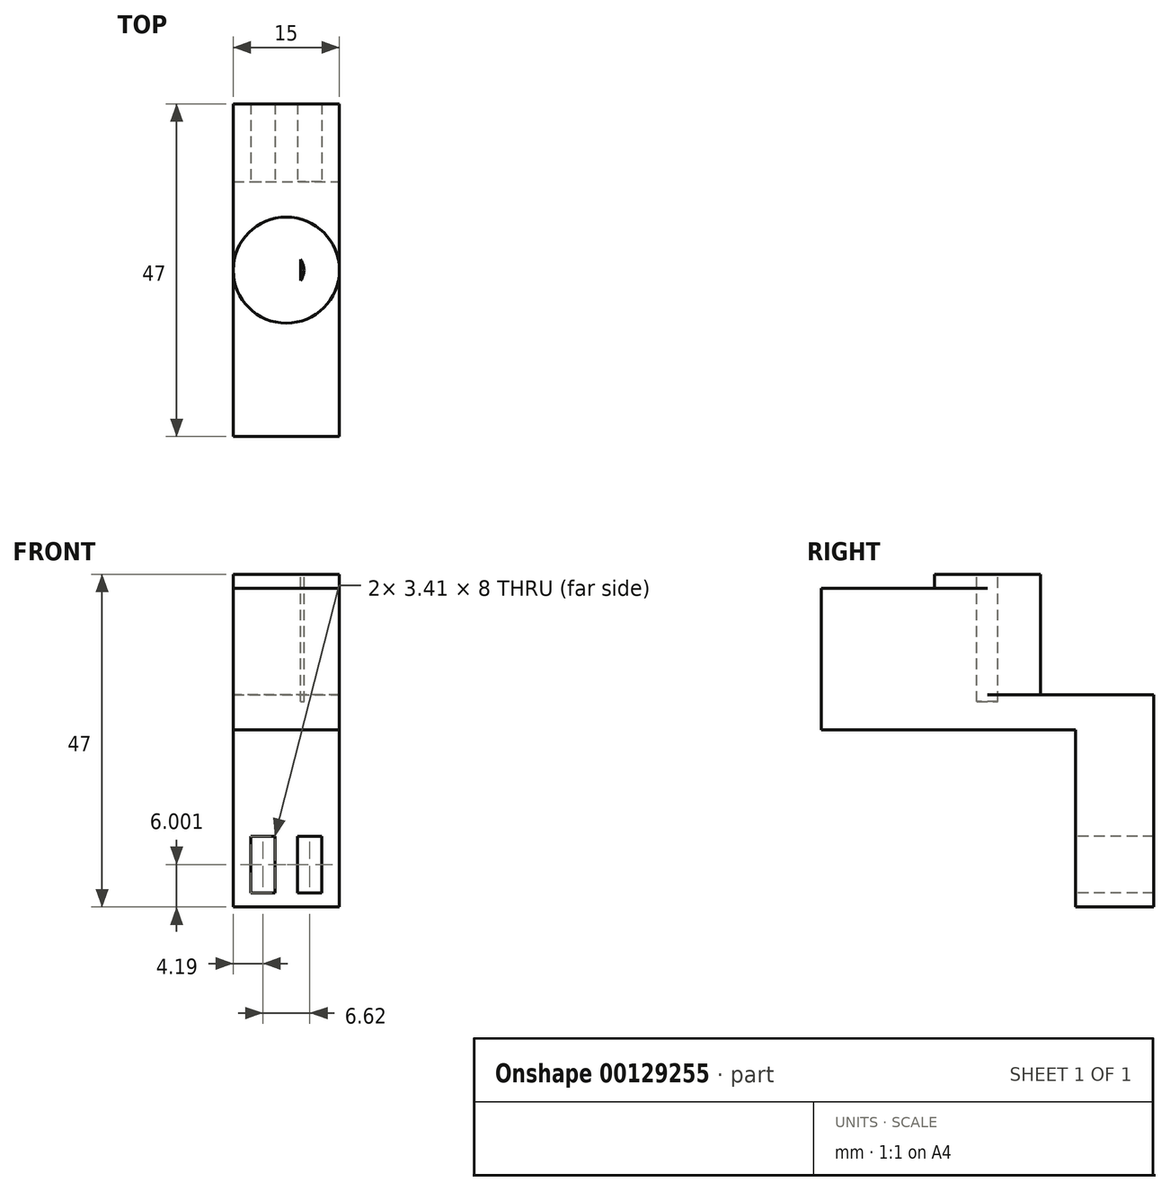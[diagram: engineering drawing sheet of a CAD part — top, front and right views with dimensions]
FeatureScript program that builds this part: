
annotation { "Feature Type Name" : "Feature", "Feature Type Description" : "" }
export const myFeature = defineFeature(function(context is Context, id is Id, definition is map)
    precondition{}
    {
        {
            var Q0;
            Q0=qCreatedBy(makeId("Top.planeOp"),FACE);
            var sketch = newSketch(context, id + "F0", { "sketchPlane" : qUnion([Q0])});
            skCircle(sketch, "E0", {"center": v(0, 0) * mm, "radius": 7.5 * mm});
            skSolve(sketch);
        }
        {
            var Q0;
            Q0=makeQuery(id+"F0.imprint","IMPRINT",FACE,{"disambiguationData":[TD([[makeQuery(id+"F0.imprint","IMPRINT",EDGE,{"derivedFrom":sQuery(id+"F0.wireOp",EDGE,"E0")}),1.0]])]});
            extrude(context, id + "F1", {"entities" : qUnion([Q0]), "depth" : 22 * mm});
        }
        {
            var Q0;
            Q0=makeQuery(id+"F1.opExtrude","CAP_FACE",FACE,{"disambiguationData":[OSD([sQuery(id+"F0.wireOp",EDGE,"E0")])],"isStart":false});
            var sketch = newSketch(context, id + "F2", { "sketchPlane" : qUnion([Q0])});
            skCircle(sketch, "E1", {"center": v(0, 0) * mm, "radius": 2.5 * mm});
            skLineSegment(sketch, "E2.bottom", {"start": v(2, 2.49) * mm, "end": v(3.01, 2.49) * mm});
            skLineSegment(sketch, "E2.top", {"start": v(2, -2.5) * mm, "end": v(3.01, -2.5) * mm});
            skLineSegment(sketch, "E2.left", {"start": v(2, 2.49) * mm, "end": v(2, -2.5) * mm});
            skLineSegment(sketch, "E2.right", {"start": v(3.01, 2.49) * mm, "end": v(3.01, -2.5) * mm});
            skSolve(sketch);
        }
        {
            var Q0;
            {var subQ0=sQuery(id+"F2.wireOp",EDGE,"E2.left");var subQ1=sQuery(id+"F2.wireOp",EDGE,"E1");var subQ2=makeQuery(id+"F2.imprint","INTERSECT",VERTEX,{"disambiguationData":[OD(0.0)],"derivedFrom":[subQ1,subQ0]});Q0=makeQuery(id+"F2.imprint","IMPRINT",FACE,{"disambiguationData":[TD([[makeQuery(id+"F2.imprint","IMPRINT",EDGE,{"disambiguationData":[TD([[subQ2,-1.0]])],"derivedFrom":subQ1}),1.0]])]});}
            extrude(context, id + "F3", {"entities" : qUnion([Q0]), "operationType" : NewBodyOperationType.REMOVE, "oppositeDirection" : true, "depth" : 18 * mm});
        }
        {
            var Q0;
            Q0=makeQuery(id+"F1.opExtrude","CAP_FACE",FACE,{"disambiguationData":[OSD([sQuery(id+"F0.wireOp",EDGE,"E0")])],"isStart":true});
            var sketch = newSketch(context, id + "F4", { "sketchPlane" : qUnion([Q0])});
            skLineSegment(sketch, "E3.bottom", {"start": v(-7.5, 0) * mm, "end": v(7.5, 0) * mm});
            skLineSegment(sketch, "E3.top", {"start": v(-7.5, -23.5) * mm, "end": v(7.5, -23.5) * mm});
            skLineSegment(sketch, "E3.left", {"start": v(-7.5, 0) * mm, "end": v(-7.5, -23.5) * mm});
            skLineSegment(sketch, "E3.right", {"start": v(7.5, 0) * mm, "end": v(7.5, -23.5) * mm});
            skLineSegment(sketch, "E4", {"start": v(-7.5, -12.48) * mm, "end": v(7.5, -12.48) * mm});
            skLineSegment(sketch, "E5.MirrorCS", {"start": v(-7.5, 12.48) * mm, "end": v(7.5, 12.48) * mm});
            skLineSegment(sketch, "E6.MirrorCS", {"start": v(-7.5, 23.5) * mm, "end": v(7.5, 23.5) * mm});
            skLineSegment(sketch, "E7.MirrorCS", {"start": v(7.5, 0) * mm, "end": v(7.5, 23.5) * mm});
            skLineSegment(sketch, "E8.MirrorCS", {"start": v(-7.5, 0) * mm, "end": v(-7.5, 23.5) * mm});
            skSolve(sketch);
        }
        {
            var Q0;
            {var subQ4=sQuery(id+"F4.wireOp",EDGE,"E4");Q0=makeQuery(id+"F4.imprint","IMPRINT",FACE,{"disambiguationData":[TD([[makeQuery(id+"F4.imprint","IMPRINT",EDGE,{"derivedFrom":subQ4}),1.0]])]});}
            var Q1;
            {var subQ0=sQuery(id+"F4.wireOp",EDGE,"E3.top");Q1=makeQuery(id+"F4.imprint","IMPRINT",FACE,{"disambiguationData":[TD([[makeQuery(id+"F4.imprint","IMPRINT",EDGE,{"derivedFrom":subQ0}),1.0]])]});}
            extrude(context, id + "F5", {"entities" : qUnion([Q0, Q1]), "operationType" : NewBodyOperationType.ADD, "oppositeDirection" : true, "depth" : 5 * mm});
        }
        {
            var Q0;
            {var subQ0=sQuery(id+"F4.wireOp",EDGE,"E3.top");Q0=makeQuery(id+"F4.imprint","IMPRINT",FACE,{"disambiguationData":[TD([[makeQuery(id+"F4.imprint","IMPRINT",EDGE,{"derivedFrom":subQ0}),1.0]])]});}
            extrude(context, id + "F6", {"entities" : qUnion([Q0]), "operationType" : NewBodyOperationType.ADD, "depth" : 25 * mm});
        }
        {
            var Q0;
            {var subQ0=sQuery(id+"F4.wireOp",EDGE,"E5.MirrorCS");Q0=makeQuery(id+"F4.imprint","IMPRINT",FACE,{"disambiguationData":[TD([[makeQuery(id+"F4.imprint","IMPRINT",EDGE,{"derivedFrom":subQ0}),-1.0]])]});}
            var Q1;
            {var subQ0=sQuery(id+"F4.wireOp",EDGE,"E5.MirrorCS");Q1=makeQuery(id+"F4.imprint","IMPRINT",FACE,{"disambiguationData":[TD([[makeQuery(id+"F4.imprint","IMPRINT",EDGE,{"derivedFrom":subQ0}),1.0]])]});}
            extrude(context, id + "F7", {"entities" : qUnion([Q0, Q1]), "operationType" : NewBodyOperationType.ADD, "oppositeDirection" : true, "depth" : 20 * mm});
        }
        {
            var Q0;
            Q0=makeQuery(id+"F6.opExtrude","SWEPT_FACE",FACE,{"disambiguationData":[OSD([sQuery(id+"F4.wireOp",EDGE,"E4")])]});
            var sketch = newSketch(context, id + "F8", { "sketchPlane" : qUnion([Q0])});
            skLineSegment(sketch, "E9", {"start": v(0, 0) * mm, "end": v(0, -31.23) * mm, "construction": true});
            skLineSegment(sketch, "E10", {"start": v(7.5, -15) * mm, "end": v(-7.5, -15) * mm, "construction": true});
            skLineSegment(sketch, "E11.bottom", {"start": v(5.02, -15) * mm, "end": v(1.6, -15) * mm});
            skLineSegment(sketch, "E11.top", {"start": v(5.02, -23) * mm, "end": v(1.6, -23) * mm});
            skLineSegment(sketch, "E11.left", {"start": v(5.02, -15) * mm, "end": v(5.02, -23) * mm});
            skLineSegment(sketch, "E11.right", {"start": v(1.6, -15) * mm, "end": v(1.6, -23) * mm});
            skLineSegment(sketch, "E12.MirrorCS", {"start": v(-5.02, -15) * mm, "end": v(-5.02, -23) * mm});
            skLineSegment(sketch, "E13.MirrorCS", {"start": v(-5.02, -23) * mm, "end": v(-1.6, -23) * mm});
            skLineSegment(sketch, "E14.MirrorCS", {"start": v(-1.6, -15) * mm, "end": v(-1.6, -23) * mm});
            skLineSegment(sketch, "E15.MirrorCS", {"start": v(-5.02, -15) * mm, "end": v(-1.6, -15) * mm});
            skSolve(sketch);
        }
        {
            var Q0;
            Q0 = qSketchRegion(id + "F8", true);
            extrude(context, id + "F9", {"entities" : qUnion([Q0]), "operationType" : NewBodyOperationType.REMOVE, "endBound" : BoundingType.THROUGH_ALL, "oppositeDirection" : true, "depth" : 25 * mm});
        }
    });
